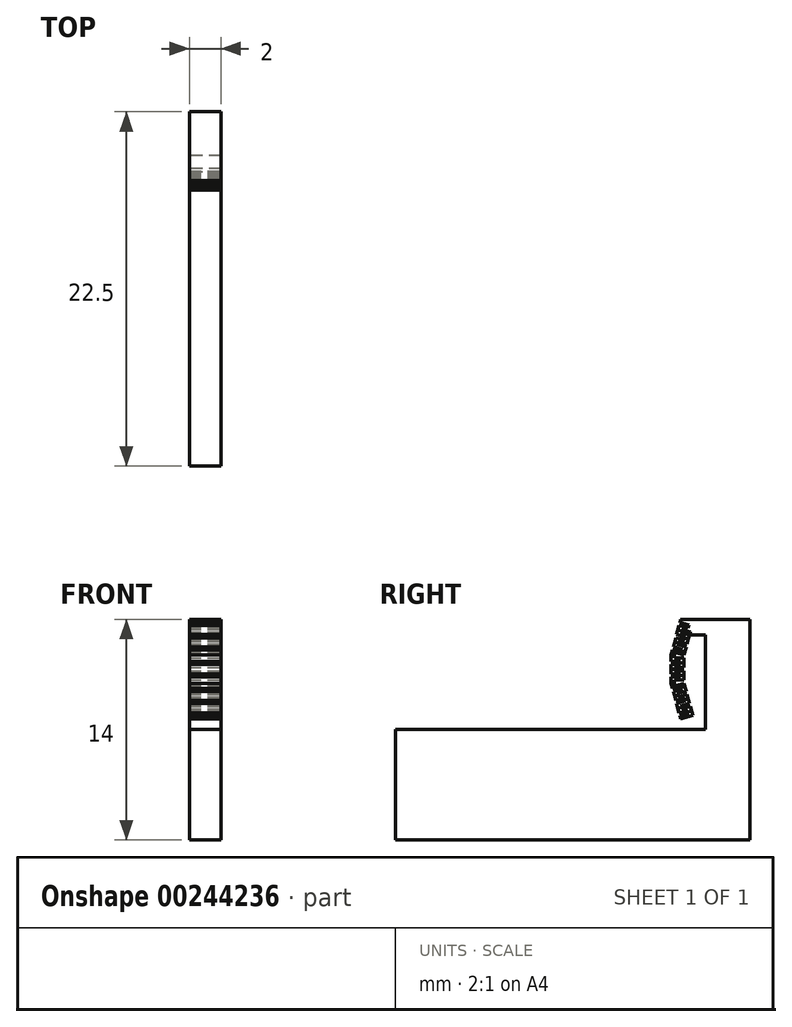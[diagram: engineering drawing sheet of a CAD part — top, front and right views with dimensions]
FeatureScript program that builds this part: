
annotation { "Feature Type Name" : "Feature", "Feature Type Description" : "" }
export const myFeature = defineFeature(function(context is Context, id is Id, definition is map)
    precondition{}
    {
        {
            assignVariable(context, id + "F0", {"name" : "thickness", "anyValue" : 2});
        }
        {
            var Q0;
            Q0=qCreatedBy(makeId("Right.planeOp"),FACE);
            var sketch = newSketch(context, id + "F1", { "sketchPlane" : qUnion([Q0])});
            skLineSegment(sketch, "E0", {"start": v(-7, 0) * mm, "end": v(15.5, 0) * mm});
            skLineSegment(sketch, "E1", {"start": v(15.5, 0) * mm, "end": v(15.5, 14) * mm});
            skLineSegment(sketch, "E2", {"start": v(12.7, 7) * mm, "end": v(-7, 7) * mm});
            skLineSegment(sketch, "E3", {"start": v(-7, 7) * mm, "end": v(-7, 0) * mm});
            skLineSegment(sketch, "E4", {"start": v(-9.03, 8.55) * mm, "end": v(17.3, 8.55) * mm, "construction": true});
            skLineSegment(sketch, "E5", {"start": v(15.5, 14) * mm, "end": v(11.1, 14) * mm});
            skLineSegment(sketch, "E6", {"start": v(11.1, 14) * mm, "end": v(10.5, 11.75) * mm});
            skLineSegment(sketch, "E7", {"start": v(10.5, 11.75) * mm, "end": v(10.5, 9.94) * mm});
            skLineSegment(sketch, "E8", {"start": v(10.5, 10.84) * mm, "end": v(13.6, 10.84) * mm, "construction": true});
            skLineSegment(sketch, "E9.MirrorCS", {"start": v(11.1, 7.69) * mm, "end": v(10.5, 9.94) * mm});
            skPoint(sketch, "E10", {"position": v(10.87, 8.55) * mm});
            skLineSegment(sketch, "E11.0", {"start": v(11.88, 7.9) * mm, "end": v(11.3, 10.04) * mm});
            skLineSegment(sketch, "E11.1", {"start": v(11.3, 11.64) * mm, "end": v(11.3, 10.04) * mm});
            skLineSegment(sketch, "E11.2", {"start": v(11.66, 13) * mm, "end": v(11.3, 11.64) * mm});
            skLineSegment(sketch, "E12", {"start": v(11.1, 7.69) * mm, "end": v(11.88, 7.9) * mm});
            skLineSegment(sketch, "E13", {"start": v(12.7, 7) * mm, "end": v(12.7, 13) * mm});
            skLineSegment(sketch, "E14", {"start": v(12.7, 13) * mm, "end": v(11.66, 13) * mm});
            skLineSegment(sketch, "E15", {"start": v(11.1, 14) * mm, "end": v(0, 14) * mm, "construction": true});
            skPoint(sketch, "E16", {"position": v(0, 7) * mm});
            skLineSegment(sketch, "E17.0", {"start": v(11.44, 7.99) * mm, "end": v(10.9, 10) * mm, "construction": true});
            skLineSegment(sketch, "E17.1", {"start": v(10.9, 11.7) * mm, "end": v(10.9, 10) * mm, "construction": true});
            skLineSegment(sketch, "E17.2", {"start": v(11.49, 13.9) * mm, "end": v(10.9, 11.7) * mm, "construction": true});
            skSolve(sketch);
        }
        {
            var Q0;
            Q0 = qSketchRegion(id + "F1", true);
            extrude(context, id + "F2", {"entities" : qUnion([Q0]), "endBound" : BoundingType.SYMMETRIC, "depth" : (getVariable(context, 'thickness')) * mm});
        }
        {
            var Q0;
            Q0=qCreatedBy(makeId("Right.planeOp"),FACE);
            var sketch = newSketch(context, id + "F3", { "sketchPlane" : qUnion([Q0])});
            skLineSegment(sketch, "E18", {"start": v(0, 0) * mm, "end": v(0, 7) * mm, "construction": true});
            skPoint(sketch, "E19", {"position": v(0, 7) * mm});
            skSolve(sketch);
        }
        {
            var Q0;
            Q0=makeQuery(id+"F2.opExtrude","CAP_FACE",FACE,{"disambiguationData":[OSD([sQuery(id+"F1.wireOp",EDGE,"E0"),sQuery(id+"F1.wireOp",EDGE,"E1"),sQuery(id+"F1.wireOp",EDGE,"E2"),sQuery(id+"F1.wireOp",EDGE,"E3"),sQuery(id+"F1.wireOp",EDGE,"E5"),sQuery(id+"F1.wireOp",EDGE,"E6"),sQuery(id+"F1.wireOp",EDGE,"E7"),sQuery(id+"F1.wireOp",EDGE,"E9.MirrorCS"),sQuery(id+"F1.wireOp",EDGE,"E11.0"),sQuery(id+"F1.wireOp",EDGE,"E11.1"),sQuery(id+"F1.wireOp",EDGE,"E11.2"),sQuery(id+"F1.wireOp",EDGE,"E12"),sQuery(id+"F1.wireOp",EDGE,"E13"),sQuery(id+"F1.wireOp",EDGE,"E14")])],"isStart":false});
            var sketch = newSketch(context, id + "F4", { "sketchPlane" : qUnion([Q0])});
            skLineSegment(sketch, "E20", {"start": v(11, 8.08) * mm, "end": v(11.58, 8.23) * mm});
            skLineSegment(sketch, "E21", {"start": v(11.58, 8.23) * mm, "end": v(11.63, 8.04) * mm});
            skLineSegment(sketch, "E22", {"start": v(11.63, 8.04) * mm, "end": v(11.05, 7.88) * mm});
            skLineSegment(sketch, "E23", {"start": v(11.05, 7.88) * mm, "end": v(11, 8.08) * mm});
            skLineSegment(sketch, "E24", {"start": v(11.72, 8.48) * mm, "end": v(11.14, 8.32) * mm});
            skLineSegment(sketch, "E25", {"start": v(11.14, 8.32) * mm, "end": v(11.09, 8.51) * mm});
            skLineSegment(sketch, "E26", {"start": v(11.09, 8.51) * mm, "end": v(11.67, 8.67) * mm});
            skLineSegment(sketch, "E27", {"start": v(11.67, 8.67) * mm, "end": v(11.72, 8.48) * mm});
            skLineSegment(sketch, "E28.1.0.0", {"start": v(11.42, 8.81) * mm, "end": v(10.84, 8.65) * mm});
            skLineSegment(sketch, "E28.1.0.1", {"start": v(11.37, 9) * mm, "end": v(11.42, 8.81) * mm});
            skLineSegment(sketch, "E28.1.0.2", {"start": v(10.93, 9.1) * mm, "end": v(10.88, 9.29) * mm});
            skLineSegment(sketch, "E28.1.0.3", {"start": v(10.84, 8.65) * mm, "end": v(10.8, 8.85) * mm});
            skLineSegment(sketch, "E28.1.0.4", {"start": v(11.51, 9.25) * mm, "end": v(10.93, 9.1) * mm});
            skLineSegment(sketch, "E28.1.0.5", {"start": v(10.8, 8.85) * mm, "end": v(11.37, 9) * mm});
            skLineSegment(sketch, "E28.1.0.6", {"start": v(10.88, 9.29) * mm, "end": v(11.46, 9.44) * mm});
            skLineSegment(sketch, "E28.1.0.7", {"start": v(11.46, 9.44) * mm, "end": v(11.51, 9.25) * mm});
            skLineSegment(sketch, "E28.2.0.0", {"start": v(11.22, 9.58) * mm, "end": v(10.64, 9.43) * mm});
            skLineSegment(sketch, "E28.2.0.1", {"start": v(11.16, 9.78) * mm, "end": v(11.22, 9.58) * mm});
            skLineSegment(sketch, "E28.2.0.3", {"start": v(10.64, 9.43) * mm, "end": v(10.59, 9.62) * mm});
            skLineSegment(sketch, "E28.2.0.5", {"start": v(10.59, 9.62) * mm, "end": v(11.16, 9.78) * mm});
            skLineSegment(sketch, "E28.direction1", {"start": v(11.05, 7.88) * mm, "end": v(10.84, 8.65) * mm, "construction": true});
            skLineSegment(sketch, "E29", {"start": v(11.3, 10.14) * mm, "end": v(10.7, 10.14) * mm});
            skLineSegment(sketch, "E30", {"start": v(10.5, 9.94) * mm, "end": v(11.3, 10.04) * mm, "construction": true});
            skLineSegment(sketch, "E31.MirrorCS", {"start": v(11.33, 9.95) * mm, "end": v(10.75, 9.8) * mm});
            skLineSegment(sketch, "E32", {"start": v(10.5, 10.14) * mm, "end": v(10.5, 9.94) * mm, "construction": true});
            skLineSegment(sketch, "E33", {"start": v(10.5, 9.94) * mm, "end": v(10.55, 9.74) * mm, "construction": true});
            skLineSegment(sketch, "E34.0", {"start": v(10.7, 9.97) * mm, "end": v(10.75, 9.8) * mm});
            skLineSegment(sketch, "E34.1", {"start": v(10.7, 10.14) * mm, "end": v(10.7, 9.97) * mm});
            skLineSegment(sketch, "E35", {"start": v(11.3, 10.14) * mm, "end": v(11.3, 10.04) * mm});
            skLineSegment(sketch, "E36", {"start": v(11.3, 10.04) * mm, "end": v(11.33, 9.95) * mm});
            skLineSegment(sketch, "E37", {"start": v(10.5, 10.84) * mm, "end": v(11.9, 10.84) * mm, "construction": true});
            skLineSegment(sketch, "E38", {"start": v(10.5, 10.34) * mm, "end": v(11.1, 10.34) * mm});
            skLineSegment(sketch, "E39", {"start": v(11.1, 10.34) * mm, "end": v(11.1, 10.54) * mm});
            skLineSegment(sketch, "E40", {"start": v(11.1, 10.54) * mm, "end": v(10.5, 10.54) * mm});
            skLineSegment(sketch, "E41", {"start": v(10.5, 10.54) * mm, "end": v(10.5, 10.34) * mm});
            skLineSegment(sketch, "E42", {"start": v(11.3, 10.74) * mm, "end": v(10.7, 10.74) * mm});
            skLineSegment(sketch, "E43", {"start": v(10.7, 10.74) * mm, "end": v(10.7, 10.84) * mm});
            skLineSegment(sketch, "E44", {"start": v(11.3, 10.74) * mm, "end": v(11.3, 10.84) * mm});
            skLineSegment(sketch, "E45.MirrorCS", {"start": v(11.05, 13.8) * mm, "end": v(11, 13.61) * mm});
            skLineSegment(sketch, "E46.MirrorCS", {"start": v(11.3, 10.94) * mm, "end": v(11.3, 10.84) * mm});
            skLineSegment(sketch, "E47.MirrorCS", {"start": v(11.16, 11.91) * mm, "end": v(11.22, 12.1) * mm});
            skLineSegment(sketch, "E48.MirrorCS", {"start": v(11.1, 11.14) * mm, "end": v(10.5, 11.14) * mm});
            skLineSegment(sketch, "E49.MirrorCS", {"start": v(10.93, 12.6) * mm, "end": v(10.88, 12.4) * mm});
            skLineSegment(sketch, "E50.MirrorCS", {"start": v(10.5, 11.14) * mm, "end": v(10.5, 11.34) * mm});
            skLineSegment(sketch, "E51.MirrorCS", {"start": v(10.88, 12.4) * mm, "end": v(11.46, 12.25) * mm});
            skLineSegment(sketch, "E52.MirrorCS", {"start": v(11.37, 12.69) * mm, "end": v(11.42, 12.88) * mm});
            skLineSegment(sketch, "E53.MirrorCS", {"start": v(11.1, 11.34) * mm, "end": v(11.1, 11.14) * mm});
            skLineSegment(sketch, "E54.MirrorCS", {"start": v(10.84, 13.03) * mm, "end": v(10.8, 12.84) * mm});
            skLineSegment(sketch, "E55.MirrorCS", {"start": v(11.58, 13.46) * mm, "end": v(11.63, 13.65) * mm});
            skLineSegment(sketch, "E56.MirrorCS", {"start": v(11.42, 12.88) * mm, "end": v(10.84, 13.03) * mm});
            skLineSegment(sketch, "E57.MirrorCS", {"start": v(11.14, 13.37) * mm, "end": v(11.09, 13.18) * mm});
            skLineSegment(sketch, "E58.MirrorCS", {"start": v(11.22, 12.1) * mm, "end": v(10.64, 12.26) * mm});
            skLineSegment(sketch, "E59.MirrorCS", {"start": v(11.3, 11.54) * mm, "end": v(11.3, 11.64) * mm});
            skLineSegment(sketch, "E60.MirrorCS", {"start": v(10.59, 12.07) * mm, "end": v(11.16, 11.91) * mm});
            skLineSegment(sketch, "E61.MirrorCS", {"start": v(10.64, 12.26) * mm, "end": v(10.59, 12.07) * mm});
            skLineSegment(sketch, "E62.MirrorCS", {"start": v(11.63, 13.65) * mm, "end": v(11.05, 13.8) * mm});
            skLineSegment(sketch, "E63.MirrorCS", {"start": v(11, 13.61) * mm, "end": v(11.58, 13.46) * mm});
            skLineSegment(sketch, "E64.MirrorCS", {"start": v(10.7, 11.72) * mm, "end": v(10.75, 11.9) * mm});
            skLineSegment(sketch, "E65.MirrorCS", {"start": v(11.3, 10.94) * mm, "end": v(10.7, 10.94) * mm});
            skLineSegment(sketch, "E66.MirrorCS", {"start": v(10.7, 10.94) * mm, "end": v(10.7, 10.84) * mm});
            skLineSegment(sketch, "E67.MirrorCS", {"start": v(10.5, 11.34) * mm, "end": v(11.1, 11.34) * mm});
            skLineSegment(sketch, "E68.MirrorCS", {"start": v(11.3, 11.54) * mm, "end": v(10.7, 11.54) * mm});
            skLineSegment(sketch, "E69.MirrorCS", {"start": v(11.51, 12.44) * mm, "end": v(10.93, 12.6) * mm});
            skLineSegment(sketch, "E70.MirrorCS", {"start": v(11.3, 11.64) * mm, "end": v(11.33, 11.74) * mm});
            skLineSegment(sketch, "E71.MirrorCS", {"start": v(11.09, 13.18) * mm, "end": v(11.66, 13.02) * mm});
            skLineSegment(sketch, "E72.MirrorCS", {"start": v(10.7, 11.54) * mm, "end": v(10.7, 11.72) * mm});
            skLineSegment(sketch, "E73.MirrorCS", {"start": v(11.33, 11.74) * mm, "end": v(10.75, 11.9) * mm});
            skLineSegment(sketch, "E74.MirrorCS", {"start": v(11.72, 13.21) * mm, "end": v(11.14, 13.37) * mm});
            skLineSegment(sketch, "E75.MirrorCS", {"start": v(10.8, 12.84) * mm, "end": v(11.37, 12.69) * mm});
            skLineSegment(sketch, "E76.MirrorCS", {"start": v(11.46, 12.25) * mm, "end": v(11.51, 12.44) * mm});
            skLineSegment(sketch, "E77", {"start": v(11.72, 13.21) * mm, "end": v(11.72, 13) * mm});
            skLineSegment(sketch, "E78", {"start": v(11.72, 13) * mm, "end": v(11.66, 13) * mm});
            skLineSegment(sketch, "E79", {"start": v(11.66, 13) * mm, "end": v(11.66, 13.02) * mm});
            skSolve(sketch);
        }
        {
            var Q0;
            Q0=qSketchRegion(id+"F4",true);
            extrude(context, id + "F5", {"entities" : qUnion([Q0]), "operationType" : NewBodyOperationType.REMOVE, "endBound" : BoundingType.UP_TO_NEXT, "oppositeDirection" : true, "depth" : 25 * mm});
        }
    });
